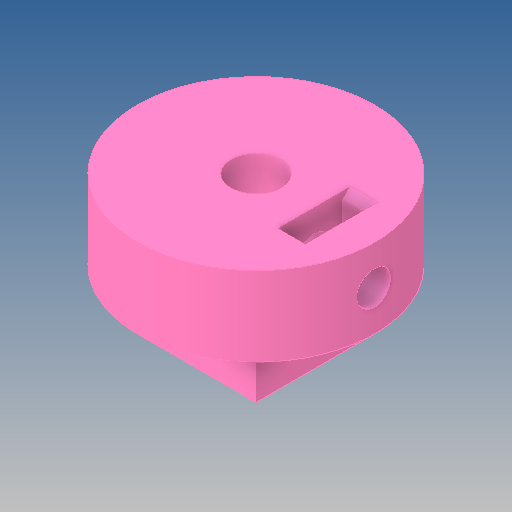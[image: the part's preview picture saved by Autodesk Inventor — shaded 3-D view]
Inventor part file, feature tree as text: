
AUTODESK INVENTOR PART (.ipt)
format: ipt  version: 2017 (Build 210142000, 142)  size: 195,072 bytes
history: native  units: mm
features: extrude x4, sketch x3, chamfer x2, other x1, projected_geometry x1
ambient origin geometry x8: Origin, YZ Plane, XZ Plane, XY Plane, X Axis, Y Axis, Z Axis, Center Point
bodies: Body1 (feature_tree)
feature tree (11):
  other  "Sólido1"
  extrude  "Extrusión1"  Depth=11.85mm
  sketch  "Boceto2"  dims[d3=6.612972mm d4=3.5mm]
  extrude  "Extrusión2"  Depth=3.5mm
  extrude  "Extrusión3"  Depth=16.0mm
  extrude  "Extrusión4"  TaperAngle=120.0deg  [1 undecoded]
  chamfer  "Chaflán1"  Distance=3.8mm
  chamfer  "Chaflán3"  Distance=16.0mm
  sketch  "Boceto1"  dims[d0=6.3mm d2=11.85mm]
  projected_geometry  "Contorno proyectado1"
  sketch  "Boceto3"  dims[d5=10.0mm d6=0.0mm d7=4.2mm d8=120.0deg d9=3.8mm d10=16.0mm d11=0.0mm d12=4.0mm d13=0.0mm d14=8.0mm d15=0.0mm d16=30.0mm d18=360.0deg d23=1.0mm d24=2.0mm d25=45.0deg d26=30.0mm d27=4.175mm d28=4.175mm d32=16.0mm d33=55.0mm d36=1.0mm d37=2.0mm d38=45.0deg]
note: 1 required parameter value undecoded (feature->parameter linkage not recoverable at this tier; creation-order binding heuristic only, values carry confidence <= 0.55)
